# Revit family: Gripple Brackets
name_source: partatom
category: Specialty Equipment
revit_build: Autodesk Revit 2017 (Build: 20160606_1515(x64)
units: mm (PartAtom-declared; Revit-internal decimal feet)

## family parameters
Always vertical = Yes
Cut with Voids When Loaded = Yes
Part Type = Normal
Room Calculation Point = No
Round Connector Dimension = Use Diameter
Shared = Yes
Work Plane-Based = Yes

## types (11) — shared parameters
Default Elevation = 1219 mm
Manufacturer = Gripple Ltd
URL = http://www.gripple.co.uk

## per-type parameters (varying)
| type | #slots | +L | -L | Length |
| PB240 | 2 | 120 mm  [stored 0.393701 ft] | -120 mm | 240 mm  [stored 0.787402 ft] |
| PB340 | 3 | 170 mm  [stored 0.557743 ft] | -170 mm | 340 mm  [stored 1.11549 ft] |
| PB440 | 4 | 220 mm  [stored 0.721785 ft] | -220 mm | 440 mm |
| PB540 | 5 | 270 mm  [stored 0.885827 ft] | -270 mm | 540 mm |
| PB640 | 6 | 320 mm  [stored 1.04987 ft] | -320 mm  [stored -1.04987 ft] | 640 mm  [stored 2.09974 ft] |
| PB740 | 7 | 370 mm | -370 mm | 740 mm |
| PB840 | 8 | 420 mm | -420 mm | 840 mm |
| PB940 | 9 | 470 mm | -470 mm | 940 mm |
| PB1040 | 10 | 520 mm | -520 mm | 1040 mm |
| PB1140 | 11 | 570 mm | -570 mm | 1140 mm |
| PB1240 | 12 | 620 mm | -620 mm  [stored -2.03412 ft] | 1240 mm |

note: column(s) folded — value = type name in every type: Assembly Code, Model

note: [stored X ft] marks values corroborated as IEEE doubles in the binary element streams (Revit-internal decimal feet)

## geometry (parser evidence)
native form markers: Blend x2, Sweep x3
no freeform markers — native parametric forms only
